# Revit family: Building-IEC309Boards-GEWISS-68QDIN-DISTRIBUTION-BOARD-10MOD_BLANK
name_source: partatom
category: Attrezzatura elettrica
revit_build: Autodesk Revit 2016 (Build: 20161004_0715(x64)
units: mm (PartAtom-declared; Revit-internal decimal feet)

## family parameters
Condiviso = No
Configurazione quadro = Due colonne, circuiti in orizzontale
Host = Muro
Numero OmniClass = 23.80.30.11.17
Punto di calcolo locali = No
Quota connettore circolare = Usa diametro
Sempre verticale = Sì
Taglio con vuoti quando caricato = No
Tipo di parte = Pannello comandi
Titolo OmniClass = Distribution Boards and Control Panels

## types (1)
- GW68002N - Q-DIN 10M COP.435x220x95 BLIND IP65
    Accordance with Standards = EN 60208 - EN 60670-1 - IEC 60670-24
    Altezza da terra = 589 mm
    Carico apparente = 0 VA
    Catalogue = BUILDING
    Catalogue Range = 68 QDIN
    Classificazione carico = Altro
    Colour = Grey RAL 7035
    Descrizione = Q-DIN 10M COP.435x220x95 BLIND IP65
    Dispersible power A (W) = 16
    Dispersible power B (W) = 42
    EAN code = 8011564744738
    Electrocod = 2242
    Glow Wire Test = 650°C
    Houseable socket = Blank lid
    IDF = 5341b2a5-b902-4f80-ae8c-9d5b282bb473
    IDT = 5251850b-27dc-44a4-affc-d4abd1ca87ad
    IP degree = IP65
    Immagine tipo = GW68002N.jpg
    Installation type = Surface-mounting
    Insulation class = II
    Modello = GW68002N
    No. of modules EN 50022 = 10
    No. of provided blank lids = -
    Numero poli = 3
    Operating temperature: = -25 +40 °C
    Potenza = 400 V
    Presa = GEWISS - Grigio RAL - 7035
    Produttore = GEWISS S.p.A.
    SEO = Board
    Shock resistance = IK09
    Spessore = 96 mm  [stored 0.314961 ft]
    Struttura = GEWISS - Grigio RAL - 7035
    Technical sheet = https://www.gewiss.com
    Thermo-pressure with ball = 70
    URL = https://www.gewiss.com
    Version file RFA = 18.0
    Version type = Empty
    Vetro = GEWISS - vetro
    Voltaggio = 400V

note: source unit labels omitted for Thermo-pressure with ball — the stored unit's dimension contradicts the parameter name (converter mislabeling)

note: [stored X ft] marks values corroborated as IEEE doubles in the binary element streams (Revit-internal decimal feet)

## geometry (parser evidence)
native form markers: Blend x2, Sweep x3
no freeform markers — native parametric forms only
